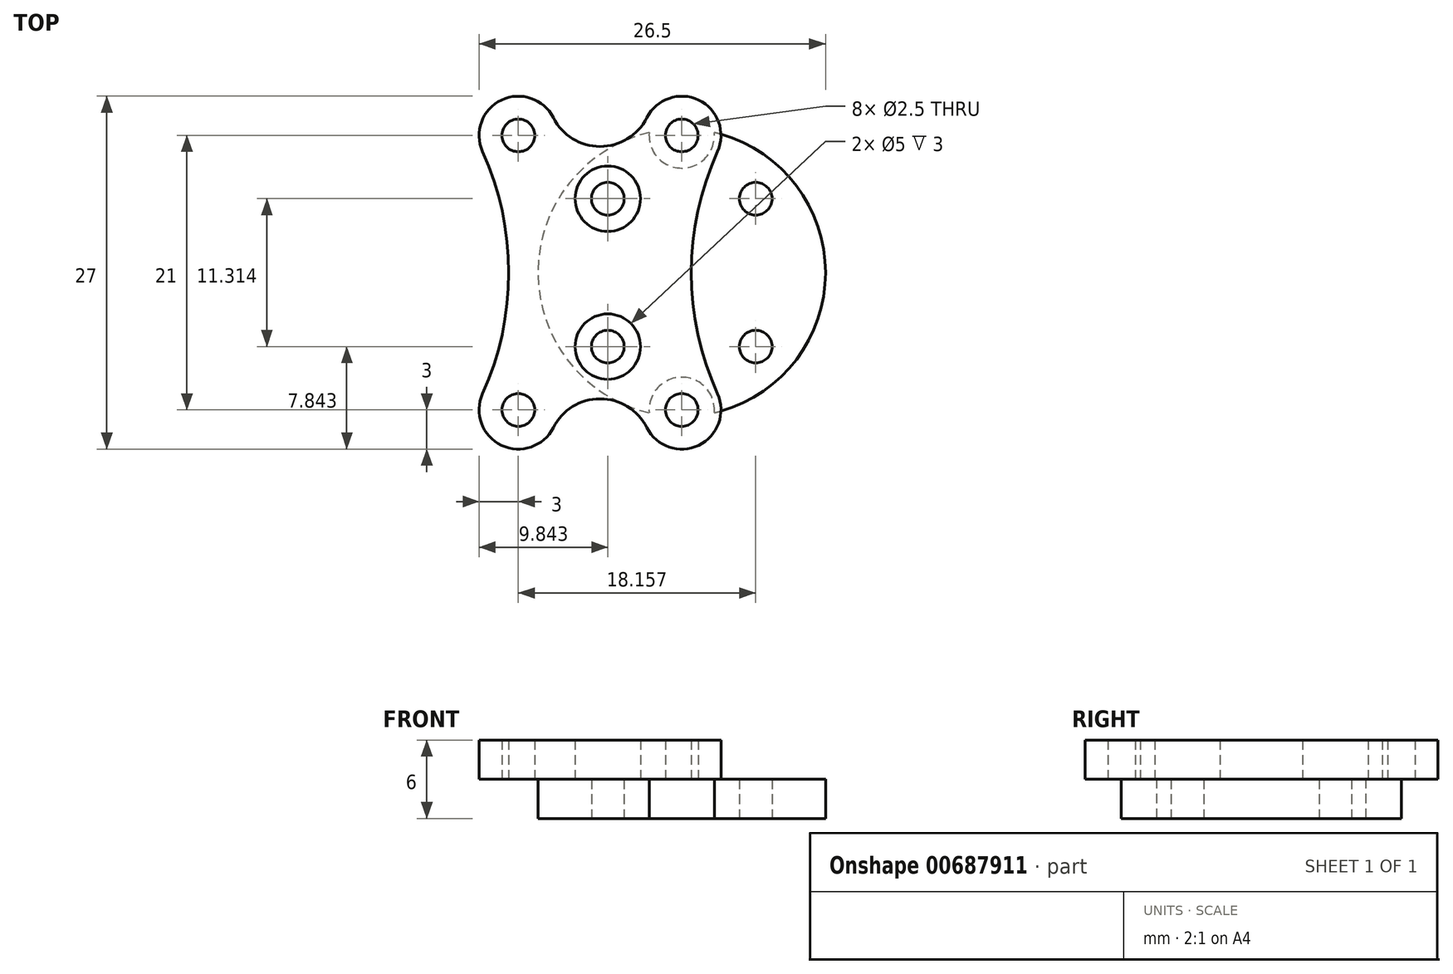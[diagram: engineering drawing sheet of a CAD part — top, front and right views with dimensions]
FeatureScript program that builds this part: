
annotation { "Feature Type Name" : "Feature", "Feature Type Description" : "" }
export const myFeature = defineFeature(function(context is Context, id is Id, definition is map)
    precondition{}
    {
        {
            var Q0;
            Q0=qCreatedBy(makeId("Top.planeOp"),FACE);
            var sketch = newSketch(context, id + "F0", { "sketchPlane" : qUnion([Q0])});
            skCircle(sketch, "E0", {"center": v(0, 0) * mm, "radius": 11 * mm});
            skCircle(sketch, "E1", {"center": v(-5.66, -5.66) * mm, "radius": 1.25 * mm});
            skLineSegment(sketch, "E2", {"start": v(-5.66, -5.66) * mm, "end": v(0, 0) * mm, "construction": true});
            skCircle(sketch, "E3.1.0", {"center": v(5.66, -5.66) * mm, "radius": 1.25 * mm});
            skCircle(sketch, "E3.2.0", {"center": v(5.66, 5.66) * mm, "radius": 1.25 * mm});
            skCircle(sketch, "E3.3.0", {"center": v(-5.66, 5.66) * mm, "radius": 1.25 * mm});
            skSolve(sketch);
        }
        {
            var Q0;
            Q0=makeQuery(id+"F0.imprint","IMPRINT",FACE,{"disambiguationData":[TD([[makeQuery(id+"F0.imprint","IMPRINT",EDGE,{"derivedFrom":sQuery(id+"F0.wireOp",EDGE,"E0")}),1.0]])]});
            extrude(context, id + "F1", {"entities" : qUnion([Q0]), "depth" : 3 * mm, "offsetDistance" : 25 * mm});
        }
        {
            var Q0;
            Q0=makeQuery(id+"F1.opExtrude","CAP_FACE",FACE,{"disambiguationData":[OSD([sQuery(id+"F0.wireOp",EDGE,"E0"),sQuery(id+"F0.wireOp",EDGE,"E1"),sQuery(id+"F0.wireOp",EDGE,"E3.1.0"),sQuery(id+"F0.wireOp",EDGE,"E3.2.0"),sQuery(id+"F0.wireOp",EDGE,"E3.3.0")])],"isStart":false});
            var sketch = newSketch(context, id + "F2", { "sketchPlane" : qUnion([Q0])});
            skCircle(sketch, "E4", {"center": v(0, -10.5) * mm, "radius": 1.25 * mm});
            skCircle(sketch, "E5.1.0.0", {"center": v(-12.5, -10.5) * mm, "radius": 1.25 * mm});
            skLineSegment(sketch, "E5.direction1", {"start": v(0, -10.5) * mm, "end": v(-12.5, -10.5) * mm, "construction": true});
            skCircle(sketch, "E6.MirrorC", {"center": v(-12.5, 10.5) * mm, "radius": 1.25 * mm});
            skCircle(sketch, "E7.MirrorC", {"center": v(0, 10.5) * mm, "radius": 1.25 * mm});
            skArc(sketch, "E8", {"start": v(-15.23, -9.26) * mm, "mid": v(-13.8, -13.2) * mm, "end": v(-9.82, -11.85) * mm});
            skArc(sketch, "E9", {"start": v(-9.82, 11.85) * mm, "mid": v(-13.8, 13.2) * mm, "end": v(-15.23, 9.26) * mm});
            skArc(sketch, "E10", {"start": v(2.73, 9.26) * mm, "mid": v(1.3, 13.2) * mm, "end": v(-2.68, 11.85) * mm});
            skArc(sketch, "E11", {"start": v(-15.23, -9.26) * mm, "mid": v(-13.24, 0) * mm, "end": v(-15.23, 9.26) * mm});
            skArc(sketch, "E12", {"start": v(-9.82, 11.85) * mm, "mid": v(-6.25, 9.65) * mm, "end": v(-2.68, 11.85) * mm});
            skArc(sketch, "E13", {"start": v(-2.68, -11.85) * mm, "mid": v(-6.25, -9.65) * mm, "end": v(-9.82, -11.85) * mm});
            skArc(sketch, "E14.trimOffspring", {"start": v(-2.68, -11.85) * mm, "mid": v(1.3, -13.2) * mm, "end": v(2.73, -9.26) * mm});
            skCircle(sketch, "E15", {"center": v(-5.66, -5.66) * mm, "radius": 2.5 * mm});
            skCircle(sketch, "E16", {"center": v(-5.66, 5.66) * mm, "radius": 2.5 * mm});
            skArc(sketch, "E17", {"start": v(2.73, 9.26) * mm, "mid": v(0.74, 0) * mm, "end": v(2.73, -9.26) * mm});
            skSolve(sketch);
        }
        {
            var Q0;
            Q0 = qSketchRegion(id + "F2", true);
            extrude(context, id + "F3", {"entities" : qUnion([Q0]), "operationType" : NewBodyOperationType.ADD, "depth" : 3 * mm, "offsetDistance" : 25 * mm});
        }
        {
            var Q0;
            Q0=makeQuery(id+"F3.opExtrude","CAP_FACE",FACE,{"disambiguationData":[OSD([sQuery(id+"F2.wireOp",EDGE,"E4"),sQuery(id+"F2.wireOp",EDGE,"E5.1.0.0"),sQuery(id+"F2.wireOp",EDGE,"E6.MirrorC"),sQuery(id+"F2.wireOp",EDGE,"E7.MirrorC"),sQuery(id+"F2.wireOp",EDGE,"E8"),sQuery(id+"F2.wireOp",EDGE,"E9"),sQuery(id+"F2.wireOp",EDGE,"E10"),sQuery(id+"F2.wireOp",EDGE,"E11"),sQuery(id+"F2.wireOp",EDGE,"E12"),sQuery(id+"F2.wireOp",EDGE,"E13"),sQuery(id+"F2.wireOp",EDGE,"E14.trimOffspring"),sQuery(id+"F2.wireOp",EDGE,"E15"),sQuery(id+"F2.wireOp",EDGE,"E16"),sQuery(id+"F2.wireOp",EDGE,"E17")])],"isStart":true});
            var sketch = newSketch(context, id + "F4", { "sketchPlane" : qUnion([Q0])});
            skCircle(sketch, "E18", {"center": v(0, 10.5) * mm, "radius": 2.5 * mm});
            skCircle(sketch, "E19", {"center": v(0, -10.5) * mm, "radius": 2.5 * mm});
            skSolve(sketch);
        }
        {
            var Q0;
            Q0 = qSketchRegion(id + "F4", true);
            extrude(context, id + "F5", {"entities" : qUnion([Q0]), "operationType" : NewBodyOperationType.REMOVE, "depth" : 5 * mm, "offsetDistance" : 25 * mm});
        }
    });
